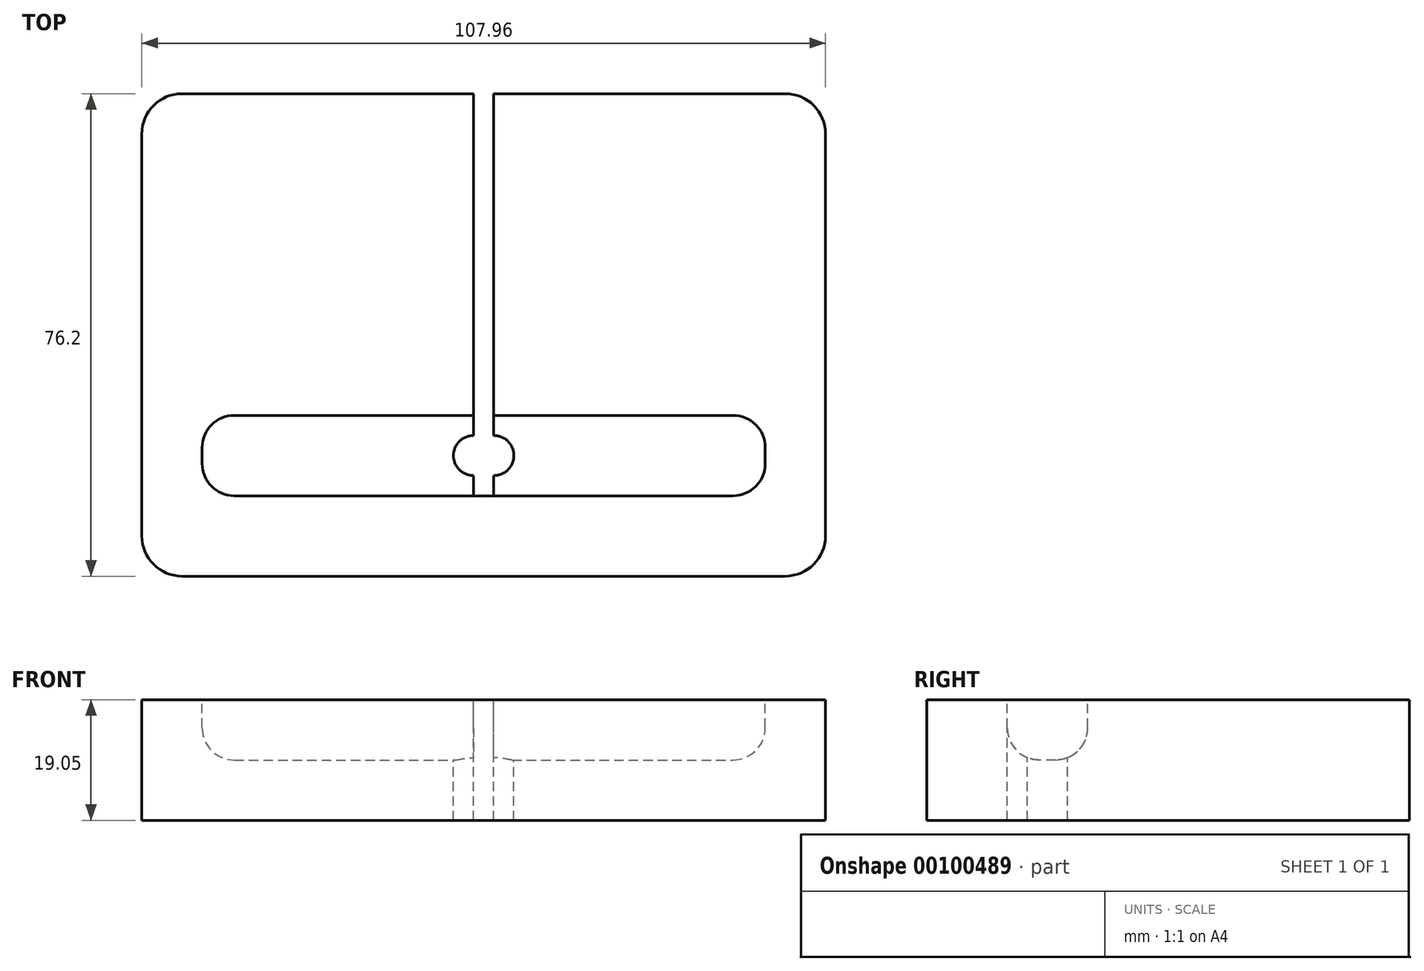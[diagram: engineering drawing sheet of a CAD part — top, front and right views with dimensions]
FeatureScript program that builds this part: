
annotation { "Feature Type Name" : "Feature", "Feature Type Description" : "" }
export const myFeature = defineFeature(function(context is Context, id is Id, definition is map)
    precondition{}
    {
        {
            var Q0;
            Q0=qCreatedBy(makeId("Top.planeOp"),FACE);
            var sketch = newSketch(context, id + "F0", { "sketchPlane" : qUnion([Q0])});
            skLineSegment(sketch, "E0.bottom", {"start": v(-53.98, 38.1) * mm, "end": v(53.98, 38.1) * mm});
            skLineSegment(sketch, "E0.top", {"start": v(-53.98, -38.1) * mm, "end": v(53.98, -38.1) * mm});
            skLineSegment(sketch, "E0.left", {"start": v(-53.97, 38.1) * mm, "end": v(-53.98, -38.1) * mm});
            skLineSegment(sketch, "E0.right", {"start": v(53.98, 38.1) * mm, "end": v(53.97, -38.1) * mm});
            skLineSegment(sketch, "E1", {"start": v(-66.53, 0) * mm, "end": v(67.03, 0) * mm, "construction": true});
            skLineSegment(sketch, "E2", {"start": v(0, 72.45) * mm, "end": v(0, -65.65) * mm, "construction": true});
            skSolve(sketch);
        }
        {
            var Q0;
            Q0=makeQuery(id+"F0.imprint","IMPRINT",FACE,{"disambiguationData":[TD([[makeQuery(id+"F0.imprint","IMPRINT",EDGE,{"derivedFrom":sQuery(id+"F0.wireOp",EDGE,"E0.bottom")}),-1.0]])]});
            extrude(context, id + "F1", {"entities" : qUnion([Q0]), "oppositeDirection" : true, "depth" : 19.05 * mm});
        }
        {
            var Q0;
            Q0=makeQuery(id+"F1.opExtrude","CAP_FACE",FACE,{"disambiguationData":[OSD([sQuery(id+"F0.wireOp",EDGE,"E0.bottom"),sQuery(id+"F0.wireOp",EDGE,"E0.top"),sQuery(id+"F0.wireOp",EDGE,"E0.left"),sQuery(id+"F0.wireOp",EDGE,"E0.right")])],"isStart":true});
            var sketch = newSketch(context, id + "F2", { "sketchPlane" : qUnion([Q0])});
            skLineSegment(sketch, "E3.bottom", {"start": v(-1.59, 38.1) * mm, "end": v(1.59, 38.1) * mm});
            skLineSegment(sketch, "E3.top", {"start": v(-1.59, -25.4) * mm, "end": v(1.59, -25.4) * mm});
            skLineSegment(sketch, "E3.left", {"start": v(-1.59, 38.1) * mm, "end": v(-1.59, -25.4) * mm});
            skLineSegment(sketch, "E3.right", {"start": v(1.59, 38.1) * mm, "end": v(1.59, -25.4) * mm});
            skLineSegment(sketch, "E4", {"start": v(0, 41.97) * mm, "end": v(0, -42.24) * mm, "construction": true});
            skSolve(sketch);
        }
        {
            var Q0;
            Q0 = qSketchRegion(id + "F2", true);
            extrude(context, id + "F3", {"entities" : qUnion([Q0]), "operationType" : NewBodyOperationType.REMOVE, "endBound" : BoundingType.THROUGH_ALL, "oppositeDirection" : true, "depth" : 25.4 * mm});
        }
        {
            var Q0;
            Q0=makeQuery(id+"F1.opExtrude","CAP_FACE",FACE,{"disambiguationData":[OSD([sQuery(id+"F0.wireOp",EDGE,"E0.bottom"),sQuery(id+"F0.wireOp",EDGE,"E0.top"),sQuery(id+"F0.wireOp",EDGE,"E0.left"),sQuery(id+"F0.wireOp",EDGE,"E0.right")])],"isStart":true});
            var sketch = newSketch(context, id + "F4", { "sketchPlane" : qUnion([Q0])});
            skLineSegment(sketch, "E5.bottom", {"start": v(-44.45, -12.7) * mm, "end": v(44.45, -12.7) * mm});
            skLineSegment(sketch, "E5.top", {"start": v(-44.45, -25.4) * mm, "end": v(44.45, -25.4) * mm});
            skLineSegment(sketch, "E5.left", {"start": v(-44.45, -12.7) * mm, "end": v(-44.45, -25.4) * mm});
            skLineSegment(sketch, "E5.right", {"start": v(44.45, -12.7) * mm, "end": v(44.45, -25.4) * mm});
            skLineSegment(sketch, "E6", {"start": v(0, 50.63) * mm, "end": v(0, -42.78) * mm, "construction": true});
            skSolve(sketch);
        }
        {
            var Q0;
            {var subQ0=sQuery(id+"F4.wireOp",EDGE,"E5.right");Q0=makeQuery(id+"F4.imprint","IMPRINT",FACE,{"disambiguationData":[TD([[makeQuery(id+"F4.imprint","IMPRINT",EDGE,{"derivedFrom":subQ0}),-1.0]])]});}
            var Q1;
            {var subQ0=sQuery(id+"F4.wireOp",EDGE,"E5.left");Q1=makeQuery(id+"F4.imprint","IMPRINT",FACE,{"disambiguationData":[TD([[makeQuery(id+"F4.imprint","IMPRINT",EDGE,{"derivedFrom":subQ0}),1.0]])]});}
            extrude(context, id + "F5", {"entities" : qUnion([Q0, Q1]), "operationType" : NewBodyOperationType.REMOVE, "oppositeDirection" : true, "depth" : 9.52 * mm});
        }
        {
            var Q0;
            Q0=makeQuery(id+"F5.boolean.opBoolean","COPY",FACE,{"derivedFrom":makeQuery(id+"F5.opExtrude","CAP_FACE",FACE,{"disambiguationData":[OSD([sQuery(id+"F2.wireOp",EDGE,"E3.right"),sQuery(id+"F4.wireOp",EDGE,"E5.bottom"),sQuery(id+"F4.wireOp",EDGE,"E5.top"),sQuery(id+"F4.wireOp",EDGE,"E5.right")])],"isStart":false})});
            var sketch = newSketch(context, id + "F6", { "sketchPlane" : qUnion([Q0])});
            skLineSegment(sketch, "E7", {"start": v(0, 53.4) * mm, "end": v(0, -70.83) * mm, "construction": true});
            skLineSegment(sketch, "E8.bottom", {"start": v(-1.59, -15.88) * mm, "end": v(1.59, -15.88) * mm});
            skLineSegment(sketch, "E8.top", {"start": v(-1.59, -22.23) * mm, "end": v(1.59, -22.23) * mm});
            skLineSegment(sketch, "E8.left", {"start": v(-4.76, -19.05) * mm, "end": v(-4.76, -19.05) * mm});
            skLineSegment(sketch, "E8.right", {"start": v(4.76, -19.05) * mm, "end": v(4.76, -19.05) * mm});
            skLineSegment(sketch, "E9", {"start": v(-63.29, -19.05) * mm, "end": v(65.8, -19.05) * mm, "construction": true});
            skPoint(sketch, "E10.visualSharp", {"position": v(-4.76, -15.88) * mm});
            skArc(sketch, "E10.filletArc", {"start": v(-1.59, -15.88) * mm, "mid": v(-3.83, -16.8) * mm, "end": v(-4.76, -19.05) * mm});
            skPoint(sketch, "E11.visualSharp", {"position": v(-4.76, -22.23) * mm});
            skArc(sketch, "E11.filletArc", {"start": v(-4.76, -19.05) * mm, "mid": v(-3.83, -21.3) * mm, "end": v(-1.59, -22.23) * mm});
            skPoint(sketch, "E12.visualSharp", {"position": v(4.76, -15.88) * mm});
            skArc(sketch, "E12.filletArc", {"start": v(4.76, -19.05) * mm, "mid": v(3.83, -16.8) * mm, "end": v(1.59, -15.88) * mm});
            skPoint(sketch, "E13.visualSharp", {"position": v(4.76, -22.23) * mm});
            skArc(sketch, "E13.filletArc", {"start": v(1.59, -22.23) * mm, "mid": v(3.83, -21.3) * mm, "end": v(4.76, -19.05) * mm});
            skSolve(sketch);
        }
        {
            var Q0;
            {var subQ1=sQuery(id+"F6.wireOp",EDGE,"E8.bottom");Q0=makeQuery(id+"F6.imprint","IMPRINT",FACE,{"disambiguationData":[TD([[makeQuery(id+"F6.imprint","IMPRINT",EDGE,{"derivedFrom":subQ1}),-1.0]])]});}
            var Q1;
            {var subQ0=sQuery(id+"F6.wireOp",EDGE,"E12.filletArc");Q1=makeQuery(id+"F6.imprint","IMPRINT",FACE,{"disambiguationData":[TD([[makeQuery(id+"F6.imprint","IMPRINT",EDGE,{"derivedFrom":subQ0}),1.0]])]});}
            extrude(context, id + "F7", {"entities" : qUnion([Q0, Q1]), "operationType" : NewBodyOperationType.REMOVE, "oppositeDirection" : true, "depth" : 12.7 * mm});
        }
        {
            var Q0;
            Q0=makeQuery(id+"F5.boolean.opBoolean","COPY",EDGE,{"derivedFrom":makeQuery(id+"F5.opExtrude","SWEPT_EDGE",EDGE,{"disambiguationData":[OSD([sQuery(id+"F4.wireOp",EDGE,"E5.bottom"),sQuery(id+"F4.wireOp",EDGE,"E5.left")])]})});
            var Q1;
            Q1=makeQuery(id+"F5.boolean.opBoolean","COPY",EDGE,{"derivedFrom":makeQuery(id+"F5.opExtrude","SWEPT_EDGE",EDGE,{"disambiguationData":[OSD([sQuery(id+"F4.wireOp",EDGE,"E5.top"),sQuery(id+"F4.wireOp",EDGE,"E5.left")])]})});
            var Q2;
            Q2=makeQuery(id+"F5.boolean.opBoolean","COPY",EDGE,{"derivedFrom":makeQuery(id+"F5.opExtrude","SWEPT_EDGE",EDGE,{"disambiguationData":[OSD([sQuery(id+"F4.wireOp",EDGE,"E5.bottom"),sQuery(id+"F4.wireOp",EDGE,"E5.right")])]})});
            var Q3;
            Q3=makeQuery(id+"F5.boolean.opBoolean","COPY",EDGE,{"derivedFrom":makeQuery(id+"F5.opExtrude","SWEPT_EDGE",EDGE,{"disambiguationData":[OSD([sQuery(id+"F4.wireOp",EDGE,"E5.top"),sQuery(id+"F4.wireOp",EDGE,"E5.right")])]})});
            fillet(context, id + "F8", {"entities" : qUnion([Q0, Q1, Q2, Q3]), "radius" : 5.08 * mm, "tangentPropagation" : true, "allowEdgeOverflow" : false});
        }
        {
            var Q0;
            {var subQ0=sQuery(id+"F4.wireOp",EDGE,"E5.bottom");Q0=makeQuery(id+"F5.boolean.opBoolean","COPY",EDGE,{"derivedFrom":makeQuery(id+"F5.opExtrude","CAP_EDGE",EDGE,{"disambiguationData":[OSD([subQ0]),TDD([makeQuery(id+"F4.imprint","IMPRINT",EDGE,{"disambiguationData":[TD([[makeQuery(id+"F4.imprint","INTERSECT",VERTEX,{"derivedFrom":[subQ0,sQuery(id+"F4.wireOp",EDGE,"E5.right")]}),1.0]])],"derivedFrom":subQ0})])],"isStart":false})});}
            fillet(context, id + "F9", {"entities" : qUnion([Q0]), "radius" : 5.08 * mm, "tangentPropagation" : true, "allowEdgeOverflow" : false});
        }
        {
            var Q0;
            {var subQ0=sQuery(id+"F4.wireOp",EDGE,"E5.bottom");Q0=makeQuery(id+"F5.boolean.opBoolean","COPY",EDGE,{"derivedFrom":makeQuery(id+"F5.opExtrude","CAP_EDGE",EDGE,{"disambiguationData":[OSD([subQ0]),TDD([makeQuery(id+"F4.imprint","IMPRINT",EDGE,{"disambiguationData":[TD([[makeQuery(id+"F4.imprint","INTERSECT",VERTEX,{"derivedFrom":[subQ0,sQuery(id+"F4.wireOp",EDGE,"E5.left")]}),-1.0]])],"derivedFrom":subQ0})])],"isStart":false})});}
            fillet(context, id + "F10", {"entities" : qUnion([Q0]), "radius" : 5.08 * mm, "tangentPropagation" : true, "allowEdgeOverflow" : false});
        }
        {
            var Q0;
            Q0=makeQuery(id+"F1.opExtrude","SWEPT_EDGE",EDGE,{"disambiguationData":[OSD([sQuery(id+"F0.wireOp",EDGE,"E0.top"),sQuery(id+"F0.wireOp",EDGE,"E0.right")])]});
            var Q1;
            Q1=makeQuery(id+"F1.opExtrude","SWEPT_EDGE",EDGE,{"disambiguationData":[OSD([sQuery(id+"F0.wireOp",EDGE,"E0.bottom"),sQuery(id+"F0.wireOp",EDGE,"E0.right")])]});
            var Q2;
            Q2=makeQuery(id+"F1.opExtrude","SWEPT_EDGE",EDGE,{"disambiguationData":[OSD([sQuery(id+"F0.wireOp",EDGE,"E0.top"),sQuery(id+"F0.wireOp",EDGE,"E0.left")])]});
            var Q3;
            Q3=makeQuery(id+"F1.opExtrude","SWEPT_EDGE",EDGE,{"disambiguationData":[OSD([sQuery(id+"F0.wireOp",EDGE,"E0.bottom"),sQuery(id+"F0.wireOp",EDGE,"E0.left")])]});
            fillet(context, id + "F11", {"entities" : qUnion([Q0, Q1, Q2, Q3]), "radius" : 6.35 * mm, "tangentPropagation" : true, "allowEdgeOverflow" : false});
        }
    });
